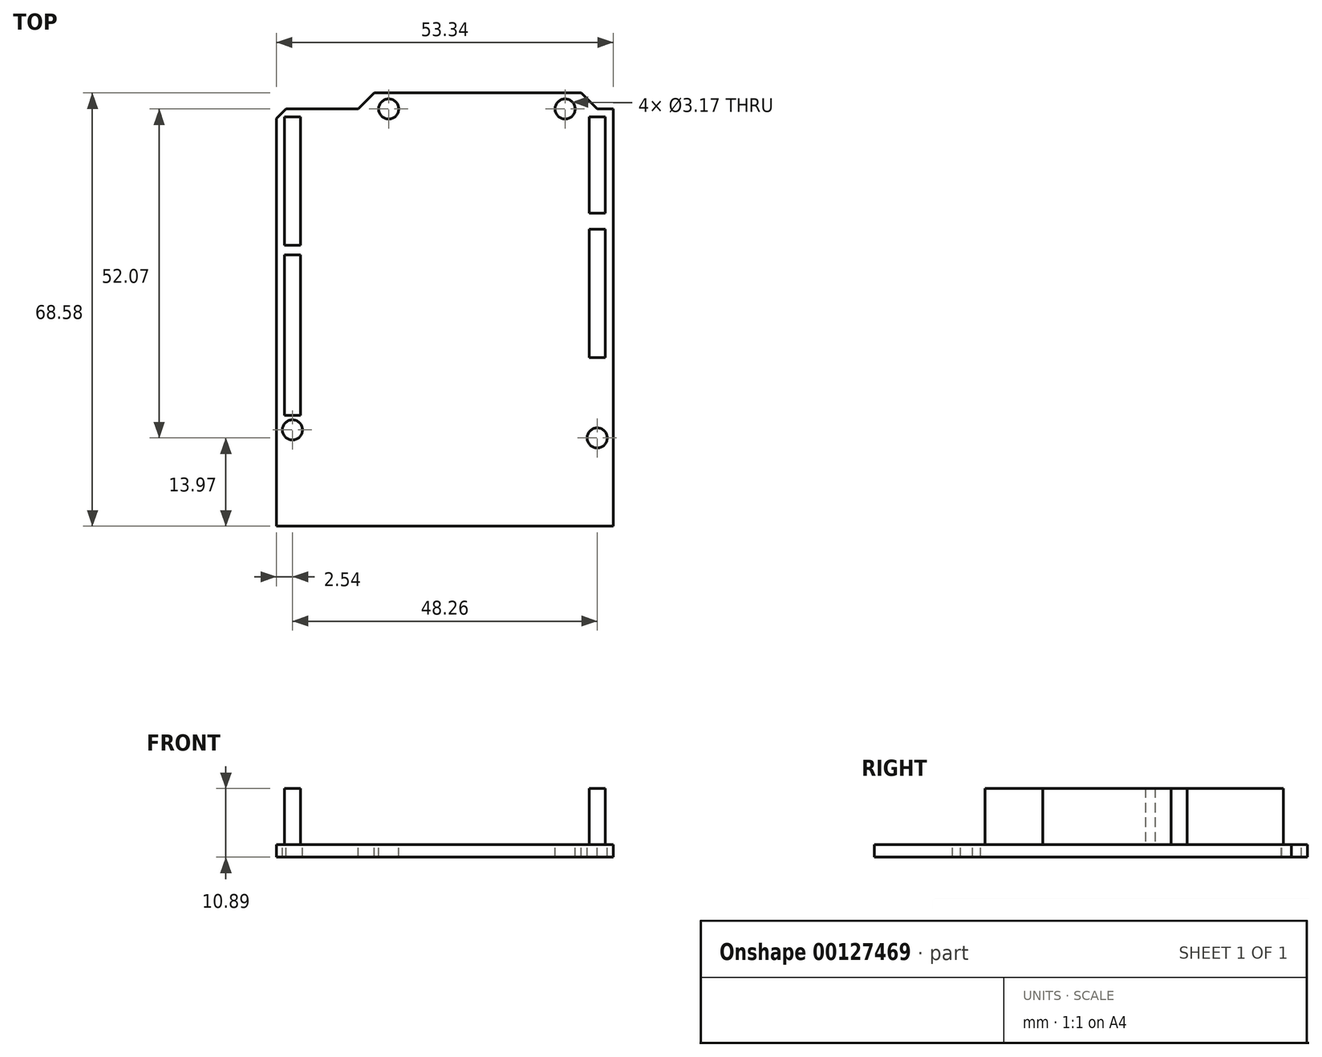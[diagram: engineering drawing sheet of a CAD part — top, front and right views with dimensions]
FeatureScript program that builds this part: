
annotation { "Feature Type Name" : "Feature", "Feature Type Description" : "" }
export const myFeature = defineFeature(function(context is Context, id is Id, definition is map)
    precondition{}
    {
        {
            var Q0;
            Q0=qCreatedBy(makeId("Top.planeOp"),FACE);
            var sketch = newSketch(context, id + "F0", { "sketchPlane" : qUnion([Q0])});
            skLineSegment(sketch, "E0.bottom", {"start": v(26.67, -34.3) * mm, "end": v(-26.67, -34.3) * mm});
            skLineSegment(sketch, "E0.top", {"start": v(26.67, 34.3) * mm, "end": v(-26.67, 34.3) * mm});
            skLineSegment(sketch, "E0.left", {"start": v(26.67, -34.3) * mm, "end": v(26.67, 34.3) * mm});
            skLineSegment(sketch, "E0.right", {"start": v(-26.67, -34.3) * mm, "end": v(-26.67, 34.29) * mm});
            skPoint(sketch, "E0.middle", {"position": v(0, 0) * mm});
            skSolve(sketch);
        }
        {
            var Q0;
            Q0 = qSketchRegion(id + "F0", true);
            extrude(context, id + "F1", {"entities" : qUnion([Q0]), "oppositeDirection" : true, "depth" : 2 * mm});
        }
        {
            var Q0;
            Q0=makeQuery(id+"F1.opExtrude","CAP_FACE",FACE,{"disambiguationData":[OSD([sQuery(id+"F0.wireOp",EDGE,"E0.bottom"),sQuery(id+"F0.wireOp",EDGE,"E0.top"),sQuery(id+"F0.wireOp",EDGE,"E0.left"),sQuery(id+"F0.wireOp",EDGE,"E0.right")])],"isStart":true});
            var sketch = newSketch(context, id + "F2", { "sketchPlane" : qUnion([Q0])});
            skLineSegment(sketch, "E1", {"start": v(-13.72, 31.75) * mm, "end": v(-11.18, 34.3) * mm});
            skLineSegment(sketch, "E2", {"start": v(-11.18, 34.3) * mm, "end": v(21.6, 34.3) * mm});
            skLineSegment(sketch, "E3", {"start": v(21.59, 34.3) * mm, "end": v(24.13, 31.75) * mm});
            skLineSegment(sketch, "E4", {"start": v(24.13, 31.75) * mm, "end": v(26.67, 31.75) * mm});
            skLineSegment(sketch, "E5", {"start": v(-13.72, 31.75) * mm, "end": v(-25.15, 31.75) * mm});
            skLineSegment(sketch, "E6", {"start": v(-25.15, 31.75) * mm, "end": v(-26.67, 30.23) * mm});
            skSolve(sketch);
        }
        {
            var Q0;
            {var subQ0=sQuery(id+"F2.wireOp",EDGE,"qWYKNfVD-uQwM-EFkf-BKra-VdrWMy3HW8Ue");Q0=makeQuery(id+"F2.imprint","IMPRINT",FACE,{"disambiguationData":[TD([[makeQuery(id+"F2.imprint","IMPRINT",EDGE,{"derivedFrom":subQ0}),1.0]])]});}
            var Q1;
            {var subQ4=sQuery(id+"F2.wireOp",EDGE,"E1");Q1=makeQuery(id+"F2.imprint","IMPRINT",FACE,{"disambiguationData":[TD([[makeQuery(id+"F2.imprint","IMPRINT",EDGE,{"derivedFrom":subQ4}),1.0]])]});}
            var Q2;
            {var subQ0=sQuery(id+"F2.wireOp",EDGE,"E3");Q2=makeQuery(id+"F2.imprint","IMPRINT",FACE,{"disambiguationData":[TD([[makeQuery(id+"F2.imprint","IMPRINT",EDGE,{"derivedFrom":subQ0}),1.0]])]});}
            extrude(context, id + "F3", {"entities" : qUnion([Q0, Q1, Q2]), "operationType" : NewBodyOperationType.REMOVE, "endBound" : BoundingType.UP_TO_NEXT, "oppositeDirection" : true, "depth" : 25.4 * mm});
        }
        {
            var Q0;
            Q0=makeQuery(id+"F1.opExtrude","CAP_FACE",FACE,{"disambiguationData":[OSD([sQuery(id+"F0.wireOp",EDGE,"E0.bottom"),sQuery(id+"F0.wireOp",EDGE,"E0.top"),sQuery(id+"F0.wireOp",EDGE,"E0.left"),sQuery(id+"F0.wireOp",EDGE,"E0.right")])],"isStart":true});
            var sketch = newSketch(context, id + "F4", { "sketchPlane" : qUnion([Q0])});
            skPoint(sketch, "E7", {"position": v(24.13, 29.21) * mm});
            skPoint(sketch, "E8.1.0.0", {"position": v(24.13, 26.67) * mm});
            skPoint(sketch, "E8.2.0.0", {"position": v(24.13, 24.13) * mm});
            skPoint(sketch, "E8.3.0.0", {"position": v(24.13, 21.6) * mm});
            skPoint(sketch, "E8.4.0.0", {"position": v(24.13, 19.05) * mm});
            skPoint(sketch, "E8.5.0.0", {"position": v(24.13, 16.51) * mm});
            skLineSegment(sketch, "E8.direction1", {"start": v(24.13, 29.21) * mm, "end": v(24.13, 26.67) * mm, "construction": true});
            skPoint(sketch, "E9", {"position": v(24.13, 11.43) * mm});
            skPoint(sketch, "E10.1.0.0", {"position": v(24.13, 8.9) * mm});
            skPoint(sketch, "E10.2.0.0", {"position": v(24.13, 6.35) * mm});
            skPoint(sketch, "E10.3.0.0", {"position": v(24.13, 3.81) * mm});
            skPoint(sketch, "E10.4.0.0", {"position": v(24.13, 1.27) * mm});
            skPoint(sketch, "E10.5.0.0", {"position": v(24.13, -1.27) * mm});
            skPoint(sketch, "E10.6.0.0", {"position": v(24.13, -3.8) * mm});
            skPoint(sketch, "E10.7.0.0", {"position": v(24.13, -6.35) * mm});
            skLineSegment(sketch, "E10.direction1", {"start": v(24.13, 11.43) * mm, "end": v(24.13, 8.9) * mm, "construction": true});
            skPoint(sketch, "E11", {"position": v(-24.13, 29.21) * mm});
            skPoint(sketch, "E12.1.0.0", {"position": v(-24.13, 26.67) * mm});
            skPoint(sketch, "E12.2.0.0", {"position": v(-24.13, 24.13) * mm});
            skPoint(sketch, "E12.3.0.0", {"position": v(-24.13, 21.59) * mm});
            skPoint(sketch, "E12.4.0.0", {"position": v(-24.13, 19.05) * mm});
            skPoint(sketch, "E12.5.0.0", {"position": v(-24.13, 16.5) * mm});
            skPoint(sketch, "E12.6.0.0", {"position": v(-24.13, 13.97) * mm});
            skPoint(sketch, "E12.7.0.0", {"position": v(-24.13, 11.43) * mm});
            skLineSegment(sketch, "E12.direction1", {"start": v(-24.13, 29.21) * mm, "end": v(-24.13, 26.67) * mm, "construction": true});
            skPoint(sketch, "E13", {"position": v(-24.13, 7.37) * mm});
            skPoint(sketch, "E14.1.0.0", {"position": v(-24.13, 4.83) * mm});
            skPoint(sketch, "E14.2.0.0", {"position": v(-24.13, 2.29) * mm});
            skPoint(sketch, "E14.3.0.0", {"position": v(-24.13, -0.25) * mm});
            skPoint(sketch, "E14.4.0.0", {"position": v(-24.13, -2.8) * mm});
            skPoint(sketch, "E14.5.0.0", {"position": v(-24.13, -5.33) * mm});
            skPoint(sketch, "E14.6.0.0", {"position": v(-24.13, -7.87) * mm});
            skPoint(sketch, "E14.7.0.0", {"position": v(-24.13, -10.41) * mm});
            skLineSegment(sketch, "E14.direction1", {"start": v(-24.13, 7.37) * mm, "end": v(-24.13, 4.83) * mm, "construction": true});
            skPoint(sketch, "E15.0.8.0", {"position": v(-24.13, -12.95) * mm});
            skPoint(sketch, "E15.0.9.0", {"position": v(-24.13, -15.5) * mm});
            skSolve(sketch);
        }
        {
            var Q0;
            Q0=qCreatedBy(makeId("Top.planeOp"),FACE);
            var sketch = newSketch(context, id + "F5", { "sketchPlane" : qUnion([Q0])});
            skPoint(sketch, "E16", {"position": v(-8.9, 31.75) * mm});
            skPoint(sketch, "E17", {"position": v(19.05, 31.75) * mm});
            skPoint(sketch, "E18", {"position": v(-24.13, -19.05) * mm});
            skPoint(sketch, "E19", {"position": v(24.13, -20.32) * mm});
            skSolve(sketch);
        }
        {
            var Q0;
            Q0=sQuery(id+"F5.wireOp",VERTEX,"E18");
            var Q1;
            Q1=sQuery(id+"F5.wireOp",VERTEX,"E19");
            var Q2;
            Q2=sQuery(id+"F5.wireOp",VERTEX,"E17");
            var Q3;
            Q3=sQuery(id+"F5.wireOp",VERTEX,"E16");
            var Q4;
            Q4=makeQuery(id+"F1.opExtrude","SWEPT_BODY",BODY,{"disambiguationData":[OSD([sQuery(id+"F0.wireOp",EDGE,"E0.bottom"),sQuery(id+"F0.wireOp",EDGE,"E0.top"),sQuery(id+"F0.wireOp",EDGE,"E0.left"),sQuery(id+"F0.wireOp",EDGE,"E0.right")])]});
            hole(context, id + "F6", {"style" : HoleStyle.SIMPLE, "endStyle" : HoleEndStyle.THROUGH, "holeDiameter" : 3.17 * mm, "locations" : qUnion([Q0, Q1, Q2, Q3]), "scope" : qUnion([Q4]), "isTappedThrough" : true});
        }
        {
            var Q0;
            Q0=makeQuery(id+"F4.imprint","IMPRINT",FACE,{"disambiguationData":[TD([[makeQuery(id+"F4.imprint","IMPRINT",EDGE,{"derivedFrom":makeQuery(id+"F1.opExtrude","CAP_EDGE",EDGE,{"disambiguationData":[OSD([sQuery(id+"F0.wireOp",EDGE,"E0.bottom")])],"isStart":true})}),-1.0]])]});
            var sketch = newSketch(context, id + "F7", { "sketchPlane" : qUnion([Q0])});
            skLineSegment(sketch, "E20.bottom", {"start": v(-25.4, 30.48) * mm, "end": v(-22.86, 30.48) * mm});
            skLineSegment(sketch, "E20.top", {"start": v(-25.4, 10.16) * mm, "end": v(-22.86, 10.16) * mm});
            skLineSegment(sketch, "E20.left", {"start": v(-25.4, 30.48) * mm, "end": v(-25.4, 10.16) * mm});
            skLineSegment(sketch, "E20.right", {"start": v(-22.86, 30.48) * mm, "end": v(-22.86, 10.16) * mm});
            skLineSegment(sketch, "E21.bottom", {"start": v(-25.4, 8.64) * mm, "end": v(-22.86, 8.64) * mm});
            skLineSegment(sketch, "E21.top", {"start": v(-25.4, -16.76) * mm, "end": v(-22.86, -16.76) * mm});
            skLineSegment(sketch, "E21.left", {"start": v(-25.4, 8.64) * mm, "end": v(-25.4, -16.76) * mm});
            skLineSegment(sketch, "E21.right", {"start": v(-22.86, 8.64) * mm, "end": v(-22.86, -16.76) * mm});
            skLineSegment(sketch, "E22.bottom", {"start": v(22.86, 30.48) * mm, "end": v(25.4, 30.48) * mm});
            skLineSegment(sketch, "E22.top", {"start": v(22.86, 15.24) * mm, "end": v(25.4, 15.24) * mm});
            skLineSegment(sketch, "E22.left", {"start": v(22.86, 30.48) * mm, "end": v(22.86, 15.24) * mm});
            skLineSegment(sketch, "E22.right", {"start": v(25.4, 30.48) * mm, "end": v(25.4, 15.24) * mm});
            skLineSegment(sketch, "E23.bottom", {"start": v(22.86, 12.7) * mm, "end": v(25.4, 12.7) * mm});
            skLineSegment(sketch, "E23.top", {"start": v(22.86, -7.62) * mm, "end": v(25.4, -7.62) * mm});
            skLineSegment(sketch, "E23.left", {"start": v(22.86, 12.7) * mm, "end": v(22.86, -7.62) * mm});
            skLineSegment(sketch, "E23.right", {"start": v(25.4, 12.7) * mm, "end": v(25.4, -7.62) * mm});
            skSolve(sketch);
        }
        {
            var Q0;
            Q0 = qSketchRegion(id + "F7", true);
            extrude(context, id + "F8", {"entities" : qUnion([Q0]), "operationType" : NewBodyOperationType.ADD, "depth" : 8.9 * mm});
        }
    });
